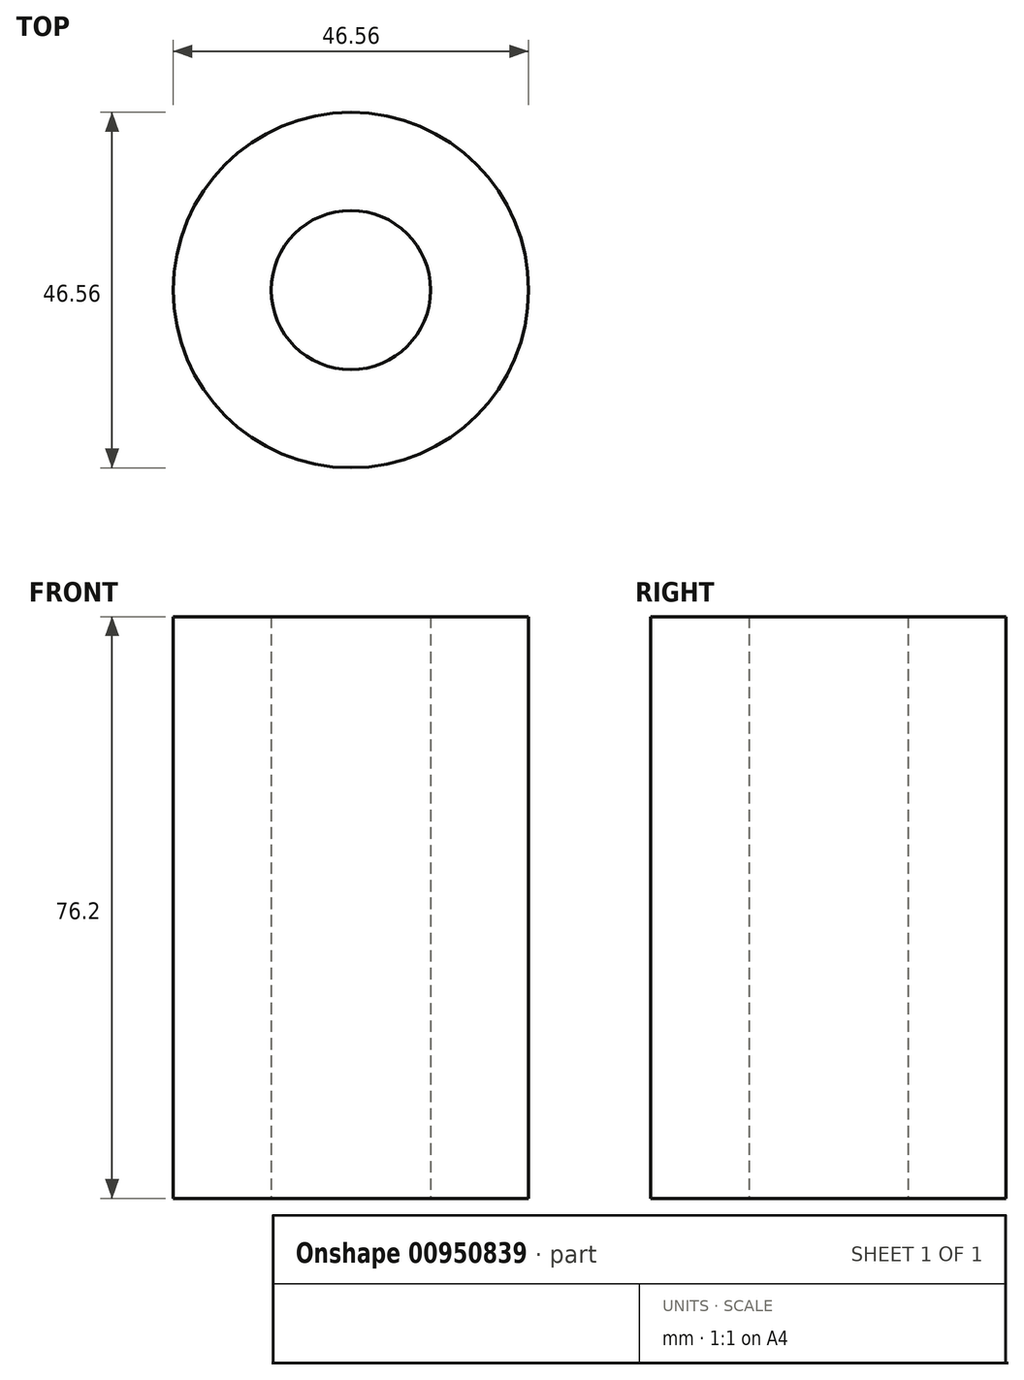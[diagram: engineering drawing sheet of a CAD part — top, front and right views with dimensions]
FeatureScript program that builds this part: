
annotation { "Feature Type Name" : "Feature", "Feature Type Description" : "" }
export const myFeature = defineFeature(function(context is Context, id is Id, definition is map)
    precondition{}
    {
        {
            var Q0;
            Q0=qCreatedBy(makeId("Top.planeOp"),FACE);
            var sketch = newSketch(context, id + "F0", { "sketchPlane" : qUnion([Q0])});
            skCircle(sketch, "E0", {"center": v(0, 0) * mm, "radius": 10.43 * mm});
            skCircle(sketch, "E1", {"center": v(0, 0) * mm, "radius": 23.28 * mm});
            skSolve(sketch);
        }
        {
            var Q0;
            Q0 = qSketchRegion(id + "F0", true);
            extrude(context, id + "F1", {"entities" : qUnion([Q0]), "depth" : 76.2 * mm, "offsetDistance" : 25.4 * mm});
        }
    });
